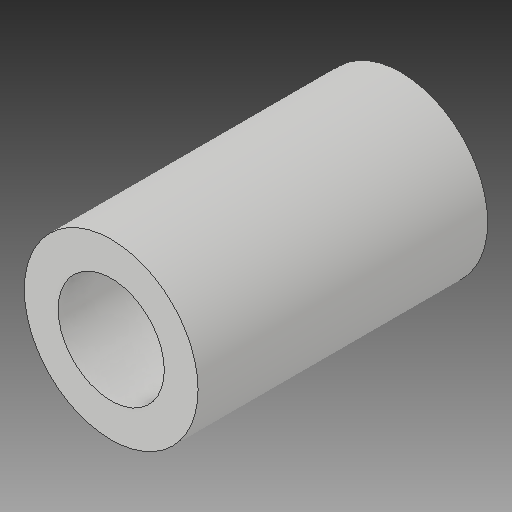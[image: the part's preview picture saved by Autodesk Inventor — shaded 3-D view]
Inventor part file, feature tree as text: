
AUTODESK INVENTOR PART (.ipt)
format: ipt  version: 2018 (Build 220112000, 112)  size: 105,472 bytes
history: native  units: mm
features: other x3, sketch x1
ambient origin geometry x8: Origin, YZ Plane, XZ Plane, XY Plane, X Axis, Y Axis, Z Axis, Center Point
bodies: Solid1 (feature_tree)
feature tree (4):
  other  "Long-Spacer.ipt"
  other  "Solid1::Long-Spacer.ipt"
  other  "TaggingFeature1"
  sketch  "Sketch1"  dims[d0=10.0mm]
